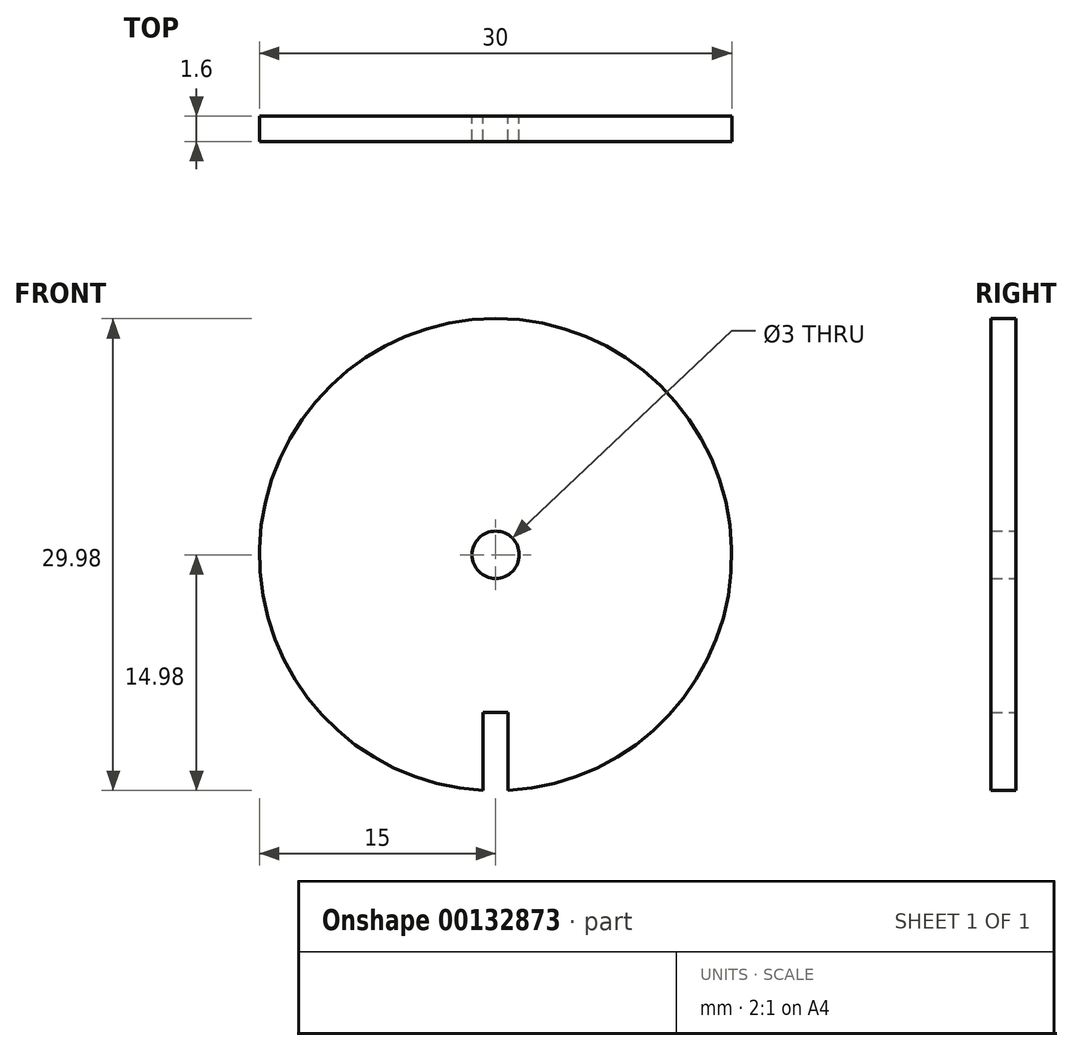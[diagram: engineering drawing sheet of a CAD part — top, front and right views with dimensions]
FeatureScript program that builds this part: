
annotation { "Feature Type Name" : "Feature", "Feature Type Description" : "" }
export const myFeature = defineFeature(function(context is Context, id is Id, definition is map)
    precondition{}
    {
        {
            var Q0;
            Q0=qCreatedBy(makeId("Front.planeOp"),FACE);
            var sketch = newSketch(context, id + "F0", { "sketchPlane" : qUnion([Q0])});
            skArc(sketch, "E0", {"start": v(0.8, -14.98) * mm, "mid": v(0, 15) * mm, "end": v(-0.8, -14.98) * mm});
            skLineSegment(sketch, "E1.bottom", {"start": v(-0.8, -10) * mm, "end": v(0.8, -10) * mm});
            skLineSegment(sketch, "E1.left", {"start": v(-0.8, -10) * mm, "end": v(-0.8, -14.98) * mm});
            skLineSegment(sketch, "E1.right", {"start": v(0.8, -10) * mm, "end": v(0.8, -14.98) * mm});
            skPoint(sketch, "E1.middle", {"position": v(0, -15) * mm});
            skCircle(sketch, "E2", {"center": v(0, 0) * mm, "radius": 1.5 * mm});
            skPoint(sketch, "E1.top.end.orphan", {"position": v(0.8, -20) * mm});
            skPoint(sketch, "E3.orphan", {"position": v(-0.8, -20) * mm});
            skLineSegment(sketch, "E4", {"start": v(-7.78, 0) * mm, "end": v(8.33, 0) * mm, "construction": true});
            skSolve(sketch);
        }
        {
            var Q0;
            Q0 = qSketchRegion(id + "F0", true);
            extrude(context, id + "F1", {"entities" : qUnion([Q0]), "depth" : 1.6 * mm});
        }
    });
